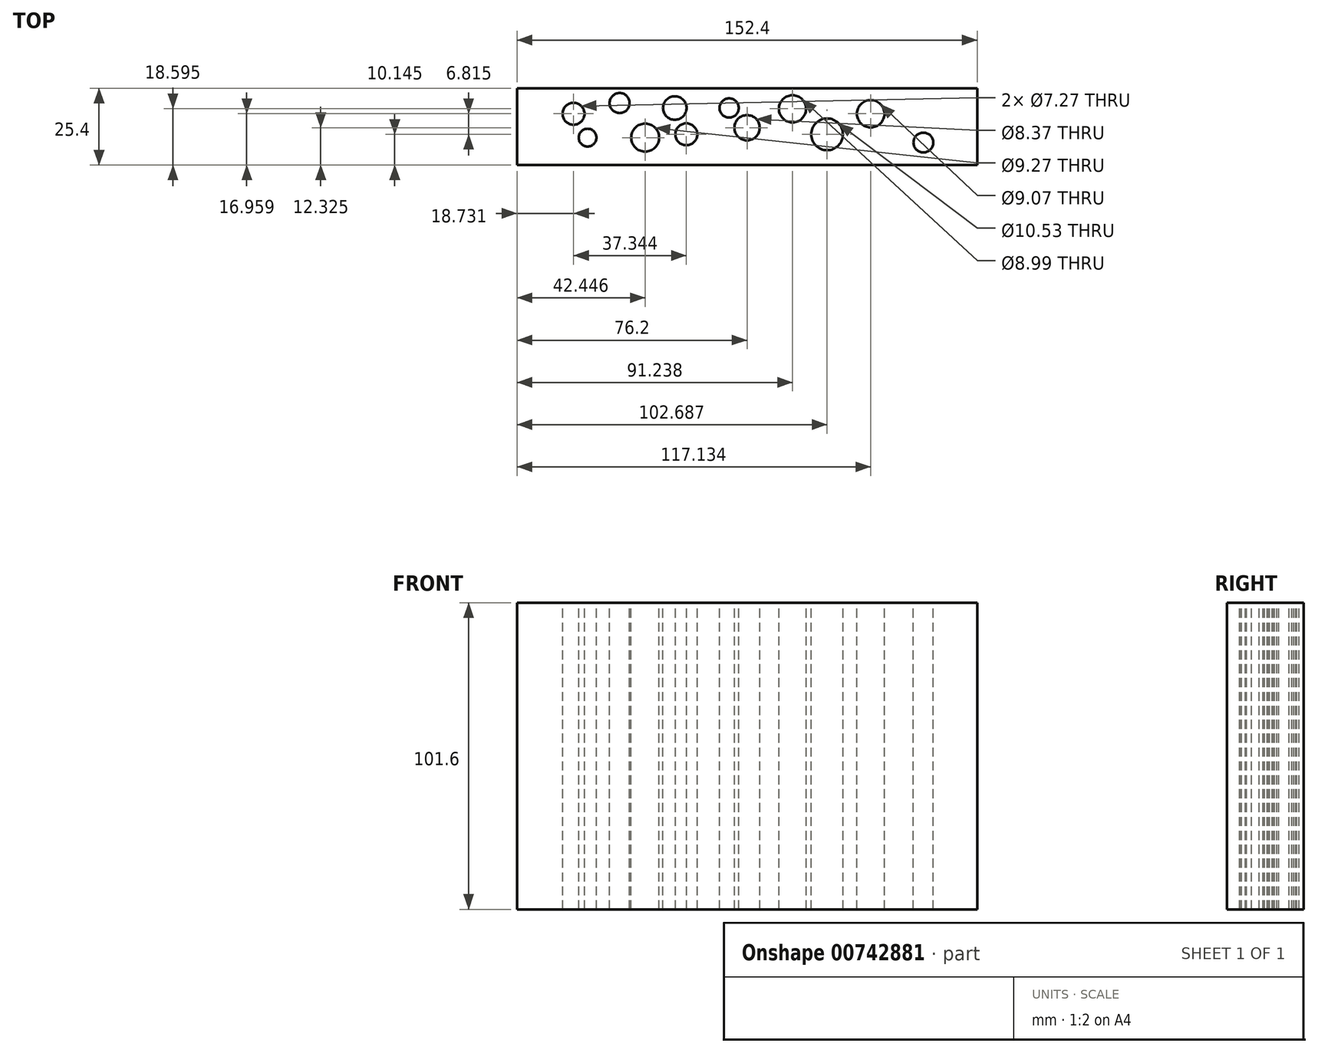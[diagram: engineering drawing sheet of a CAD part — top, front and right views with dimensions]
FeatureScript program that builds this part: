
annotation { "Feature Type Name" : "Feature", "Feature Type Description" : "" }
export const myFeature = defineFeature(function(context is Context, id is Id, definition is map)
    precondition{}
    {
        {
            var Q0;
            Q0=qCreatedBy(makeId("Front.planeOp"),FACE);
            var sketch = newSketch(context, id + "F0", { "sketchPlane" : qUnion([Q0])});
            skLineSegment(sketch, "E0.bottom", {"start": v(-76.2, 50.8) * mm, "end": v(76.2, 50.8) * mm});
            skLineSegment(sketch, "E0.top", {"start": v(-76.2, -50.8) * mm, "end": v(76.2, -50.8) * mm});
            skLineSegment(sketch, "E0.left", {"start": v(-76.2, 50.8) * mm, "end": v(-76.2, -50.8) * mm});
            skLineSegment(sketch, "E0.right", {"start": v(76.2, 50.8) * mm, "end": v(76.2, -50.8) * mm});
            skPoint(sketch, "E0.middle", {"position": v(0, 0) * mm});
            skSolve(sketch);
        }
        {
            var Q0;
            Q0=makeQuery(id+"F0.imprint","IMPRINT",FACE,{"disambiguationData":[TD([[makeQuery(id+"F0.imprint","IMPRINT",EDGE,{"derivedFrom":sQuery(id+"F0.wireOp",EDGE,"E0.bottom")}),-1.0]])]});
            extrude(context, id + "F1", {"entities" : qUnion([Q0]), "depth" : 25.4 * mm, "offsetDistance" : 25.4 * mm});
        }
        {
            var Q0;
            Q0=makeQuery(id+"F1.opExtrude","SWEPT_FACE",FACE,{"disambiguationData":[OSD([sQuery(id+"F0.wireOp",EDGE,"E0.bottom")])]});
            var sketch = newSketch(context, id + "F2", { "sketchPlane" : qUnion([Q0])});
            skCircle(sketch, "E1", {"center": v(0, -13.07) * mm, "radius": 4.19 * mm});
            skCircle(sketch, "E2", {"center": v(-57.47, -8.44) * mm, "radius": 3.64 * mm});
            skCircle(sketch, "E3", {"center": v(-33.75, -16.35) * mm, "radius": 4.63 * mm});
            skCircle(sketch, "E4", {"center": v(40.93, -8.44) * mm, "radius": 4.54 * mm});
            skCircle(sketch, "E5", {"center": v(26.49, -15.26) * mm, "radius": 5.26 * mm});
            skCircle(sketch, "E6", {"center": v(58.38, -17.98) * mm, "radius": 3.3 * mm});
            skCircle(sketch, "E7", {"center": v(15.04, -6.8) * mm, "radius": 4.5 * mm});
            skCircle(sketch, "E8", {"center": v(-23.94, -6.53) * mm, "radius": 3.9 * mm});
            skCircle(sketch, "E9", {"center": v(-20.12, -15.26) * mm, "radius": 3.64 * mm});
            skCircle(sketch, "E10", {"center": v(-52.83, -16.35) * mm, "radius": 2.94 * mm});
            skCircle(sketch, "E11", {"center": v(-42.2, -4.9) * mm, "radius": 3.32 * mm});
            skCircle(sketch, "E12", {"center": v(-5.95, -6.53) * mm, "radius": 3.18 * mm});
            skSolve(sketch);
        }
        {
            var Q0;
            Q0 = qSketchRegion(id + "F2", true);
            extrude(context, id + "F3", {"entities" : qUnion([Q0]), "operationType" : NewBodyOperationType.REMOVE, "oppositeDirection" : true, "depth" : 152.4 * mm, "offsetDistance" : 25.4 * mm});
        }
    });
